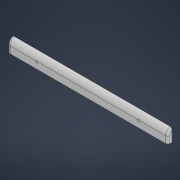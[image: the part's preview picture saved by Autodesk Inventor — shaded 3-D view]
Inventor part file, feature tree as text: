
AUTODESK INVENTOR PART (.ipt)
format: ipt  version: 2022 (Build 260153000, 153)  size: 112,640 bytes
history: native  units: in
note: dims shown in document units (in); Inventor stores cm internally (conversion verified against a paired STEP export)
features: fillet x2, extrude x1, sketch x1
ambient origin geometry x8: Origin, YZ Plane, XZ Plane, XY Plane, X Axis, Y Axis, Z Axis, Center Point
bodies: Solid1 (feature_tree)
feature tree (4):
  extrude  "Extrusion1"  Depth=0.3937in
  fillet  "Fillet1"  Radius=0.3937in
  fillet  "Fillet2"  Radius=0.7874in
  sketch  "Sketch1"  dims[d0=29.5276in d1=2.3622in d3=0.3937in d4=0.7874in d5=0.0in d6=1.1811in d7=0.3937in d8=0.0in d9=0.0in]
